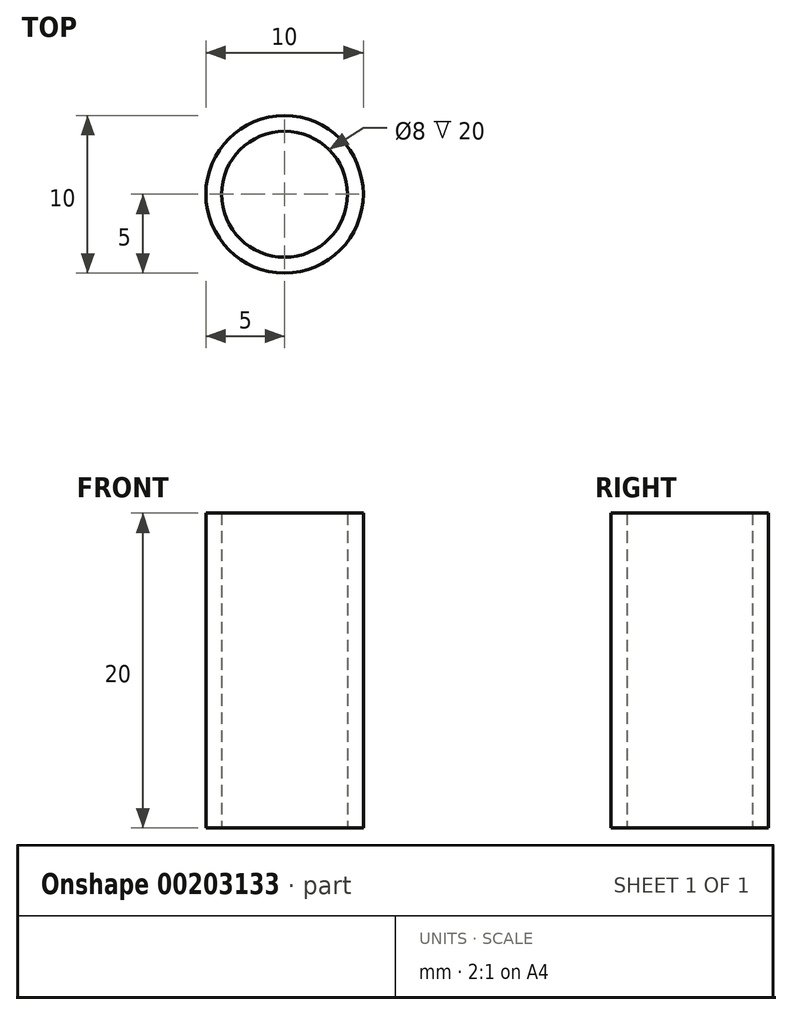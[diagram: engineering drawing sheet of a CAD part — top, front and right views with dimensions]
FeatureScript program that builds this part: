
annotation { "Feature Type Name" : "Feature", "Feature Type Description" : "" }
export const myFeature = defineFeature(function(context is Context, id is Id, definition is map)
    precondition{}
    {
        {
            var Q0;
            Q0=qCreatedBy(makeId("Top.planeOp"),FACE);
            var sketch = newSketch(context, id + "F0", { "sketchPlane" : qUnion([Q0])});
            skCircle(sketch, "E0", {"center": v(0, 0) * mm, "radius": 5 * mm});
            skCircle(sketch, "E1", {"center": v(0, 0) * mm, "radius": 4 * mm});
            skSolve(sketch);
        }
        {
            var Q0;
            Q0 = qSketchRegion(id + "F0", true);
            extrude(context, id + "F1", {"entities" : qUnion([Q0]), "depth" : 20 * mm});
        }
    });
